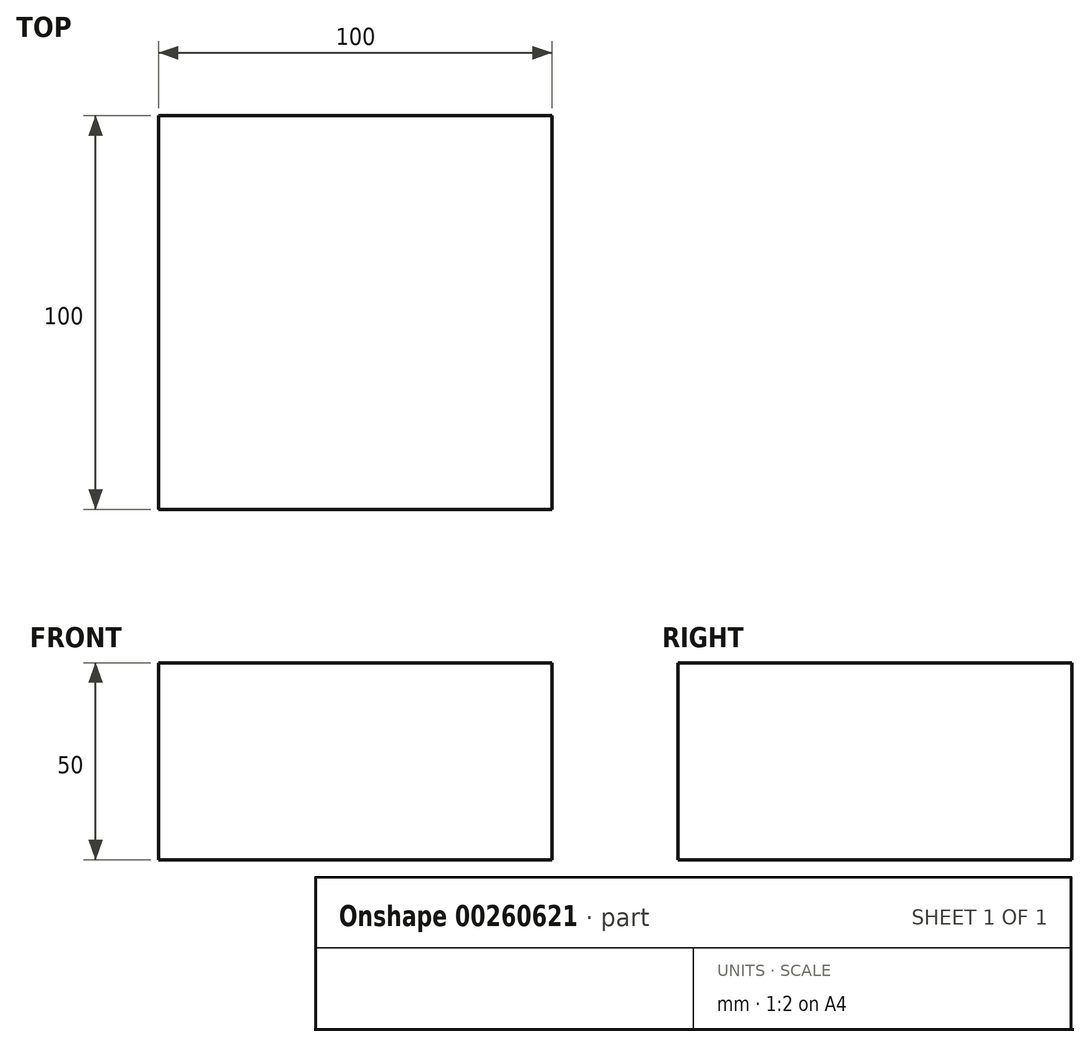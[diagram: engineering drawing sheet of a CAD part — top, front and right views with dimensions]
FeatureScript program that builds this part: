
annotation { "Feature Type Name" : "Feature", "Feature Type Description" : "" }
export const myFeature = defineFeature(function(context is Context, id is Id, definition is map)
    precondition{}
    {
        {
            var Q0;
            Q0=qCreatedBy(makeId("Top.planeOp"),FACE);
            var sketch = newSketch(context, id + "F0", { "sketchPlane" : qUnion([Q0])});
            skLineSegment(sketch, "E0.bottom", {"start": v(-50, 50) * mm, "end": v(50, 50) * mm});
            skLineSegment(sketch, "E0.top", {"start": v(-50, -50) * mm, "end": v(50, -50) * mm});
            skLineSegment(sketch, "E0.left", {"start": v(-50, 50) * mm, "end": v(-50, -50) * mm});
            skLineSegment(sketch, "E0.right", {"start": v(50, 50) * mm, "end": v(50, -50) * mm});
            skPoint(sketch, "E0.middle", {"position": v(0, 0) * mm});
            skSolve(sketch);
        }
        {
            var Q0;
            Q0=makeQuery(id+"F0.imprint","IMPRINT",FACE,{"disambiguationData":[TD([[makeQuery(id+"F0.imprint","IMPRINT",EDGE,{"derivedFrom":sQuery(id+"F0.wireOp",EDGE,"E0.bottom")}),-1.0]])]});
            extrude(context, id + "F1", {"entities" : qUnion([Q0]), "depth" : 50 * mm});
        }
    });
